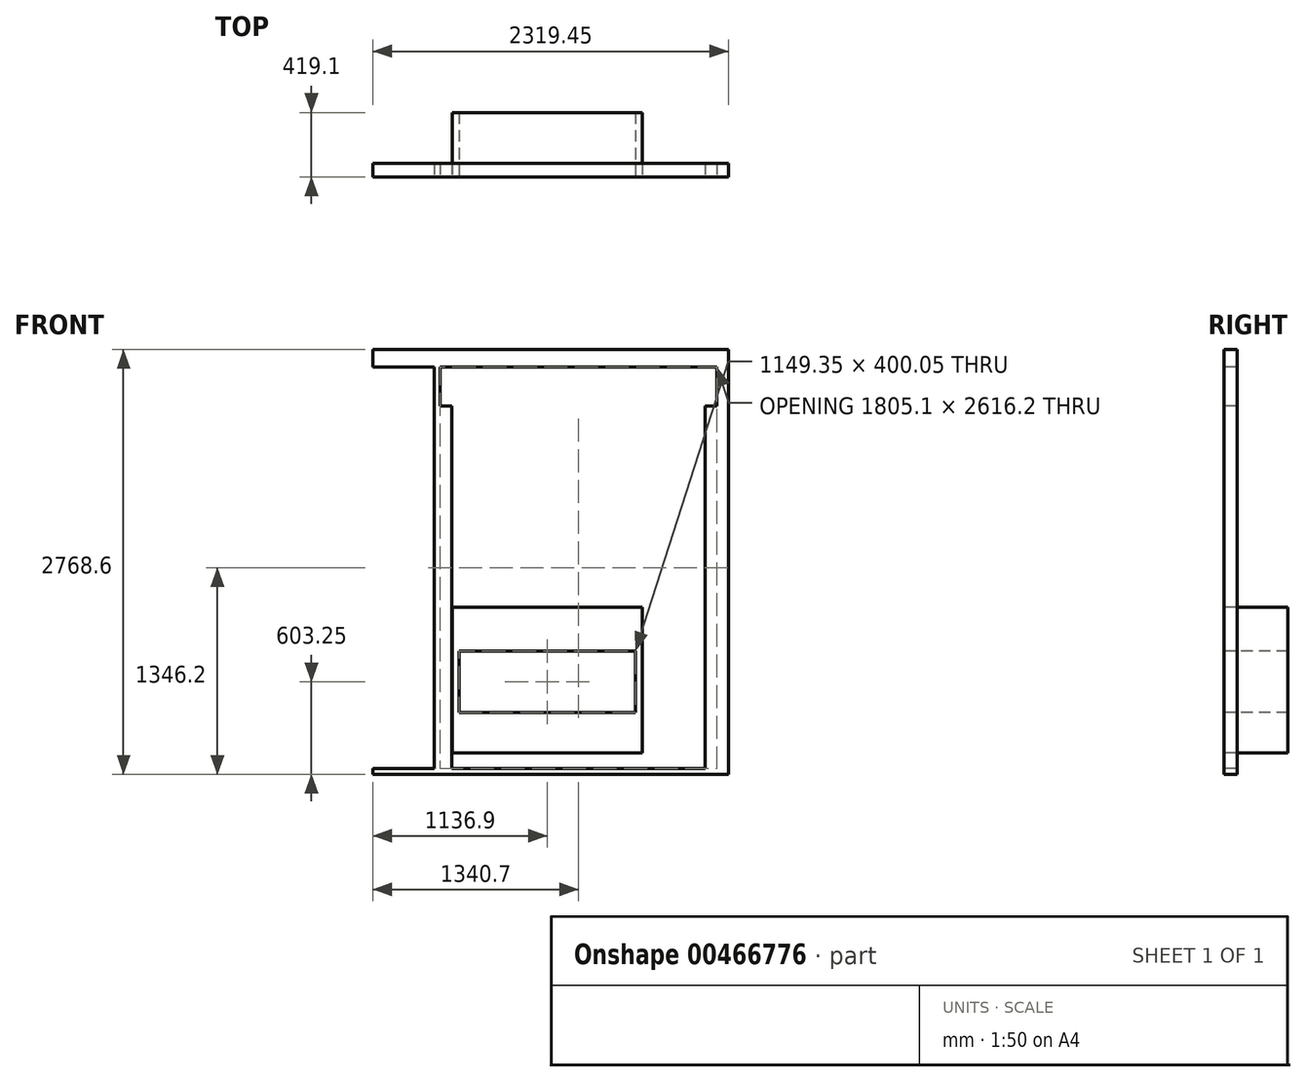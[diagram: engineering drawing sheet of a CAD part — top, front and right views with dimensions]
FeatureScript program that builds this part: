
annotation { "Feature Type Name" : "Feature", "Feature Type Description" : "" }
export const myFeature = defineFeature(function(context is Context, id is Id, definition is map)
    precondition{}
    {
        {
            var Q0;
            Q0=qCreatedBy(makeId("Front.planeOp"),FACE);
            var sketch = newSketch(context, id + "F0", { "sketchPlane" : qUnion([Q0])});
            skLineSegment(sketch, "E0", {"start": v(-619.13, 0) * mm, "end": v(-619.13, 949.33) * mm});
            skLineSegment(sketch, "E1", {"start": v(-619.13, 949.33) * mm, "end": v(619.12, 949.33) * mm});
            skLineSegment(sketch, "E2", {"start": v(619.12, 949.33) * mm, "end": v(619.12, 0) * mm});
            skLineSegment(sketch, "E3", {"start": v(619.12, 0) * mm, "end": v(-619.13, 0) * mm});
            skLineSegment(sketch, "E4.bottom", {"start": v(-574.68, 663.58) * mm, "end": v(574.67, 663.58) * mm});
            skLineSegment(sketch, "E4.top", {"start": v(-574.68, 263.53) * mm, "end": v(574.67, 263.53) * mm});
            skLineSegment(sketch, "E4.left", {"start": v(-574.68, 663.58) * mm, "end": v(-574.68, 263.53) * mm});
            skLineSegment(sketch, "E4.right", {"start": v(574.67, 663.58) * mm, "end": v(574.67, 263.53) * mm});
            skSolve(sketch);
        }
        {
            var Q0;
            Q0=qCreatedBy(makeId("Front.planeOp"),FACE);
            var sketch = newSketch(context, id + "F1", { "sketchPlane" : qUnion([Q0])});
            skLineSegment(sketch, "E5.bottom", {"start": v(-646.25, 38.1) * mm, "end": v(-684.35, 38.1) * mm});
            skLineSegment(sketch, "E5.top", {"start": v(-646.25, 2400.3) * mm, "end": v(-684.35, 2400.3) * mm});
            skLineSegment(sketch, "E5.left", {"start": v(-646.25, 38.1) * mm, "end": v(-646.25, 2400.3) * mm});
            skLineSegment(sketch, "E5.right", {"start": v(-684.35, 38.1) * mm, "end": v(-684.35, 2400.3) * mm});
            skLineSegment(sketch, "E6", {"start": v(-684.35, 38.1) * mm, "end": v(-724.15, 38.1) * mm});
            skLineSegment(sketch, "E7", {"start": v(-724.15, 38.1) * mm, "end": v(-724.15, 2400.3) * mm});
            skLineSegment(sketch, "E8", {"start": v(-724.15, 2400.3) * mm, "end": v(-684.35, 2400.3) * mm});
            skLineSegment(sketch, "E9.bottom", {"start": v(1004.75, 38.1) * mm, "end": v(1042.85, 38.1) * mm});
            skLineSegment(sketch, "E9.top", {"start": v(1004.75, 2400.3) * mm, "end": v(1042.85, 2400.3) * mm});
            skLineSegment(sketch, "E9.left", {"start": v(1004.75, 38.1) * mm, "end": v(1004.75, 2400.3) * mm});
            skLineSegment(sketch, "E9.right", {"start": v(1042.85, 38.1) * mm, "end": v(1042.85, 2400.3) * mm});
            skLineSegment(sketch, "E10", {"start": v(1042.85, 38.1) * mm, "end": v(1080.95, 38.1) * mm});
            skLineSegment(sketch, "E11", {"start": v(1080.95, 38.1) * mm, "end": v(1080.95, 2400.3) * mm});
            skLineSegment(sketch, "E12", {"start": v(1080.95, 2400.3) * mm, "end": v(1042.85, 2400.3) * mm});
            skLineSegment(sketch, "E13", {"start": v(-724.15, 38.1) * mm, "end": v(-762.25, 38.1) * mm});
            skLineSegment(sketch, "E14", {"start": v(-724.15, 2400.3) * mm, "end": v(-724.15, 2654.3) * mm});
            skLineSegment(sketch, "E15", {"start": v(-724.15, 2654.3) * mm, "end": v(-762.25, 2654.3) * mm});
            skLineSegment(sketch, "E16", {"start": v(-646.25, 2400.3) * mm, "end": v(1004.75, 2400.3) * mm});
            skLineSegment(sketch, "E17", {"start": v(-762.25, 38.1) * mm, "end": v(-762.25, 2654.3) * mm});
            skLineSegment(sketch, "E18.bottom", {"start": v(-724.15, 2654.3) * mm, "end": v(1080.95, 2654.3) * mm});
            skLineSegment(sketch, "E18.top", {"start": v(-724.15, 2400.3) * mm, "end": v(1080.95, 2400.3) * mm});
            skLineSegment(sketch, "E18.left", {"start": v(-724.15, 2654.3) * mm, "end": v(-724.15, 2400.3) * mm});
            skLineSegment(sketch, "E18.right", {"start": v(1080.95, 2654.3) * mm, "end": v(1080.95, 2400.3) * mm});
            skLineSegment(sketch, "E19.left", {"start": v(1080.95, 2654.3) * mm, "end": v(1080.95, 38.1) * mm});
            skLineSegment(sketch, "E20.top", {"start": v(1080.95, 38.1) * mm, "end": v(1119.05, 38.1) * mm});
            skLineSegment(sketch, "E21.top", {"start": v(1119.05, 38.1) * mm, "end": v(1157.15, 38.1) * mm});
            skLineSegment(sketch, "E22", {"start": v(1080.95, 2654.3) * mm, "end": v(1119.05, 2654.3) * mm});
            skLineSegment(sketch, "E23", {"start": v(1157.15, 2654.3) * mm, "end": v(1119.05, 2654.3) * mm});
            skLineSegment(sketch, "E24", {"start": v(1119.05, 2654.3) * mm, "end": v(1119.05, 38.1) * mm});
            skLineSegment(sketch, "E25", {"start": v(1119.05, 38.1) * mm, "end": v(1080.95, 38.1) * mm});
            skLineSegment(sketch, "E26", {"start": v(1157.15, 2654.3) * mm, "end": v(1157.15, 38.1) * mm});
            skLineSegment(sketch, "E27.bottom", {"start": v(-1162.3, 2692.4) * mm, "end": v(1157.15, 2692.4) * mm});
            skLineSegment(sketch, "E27.top", {"start": v(-1162.3, 2654.3) * mm, "end": v(1157.15, 2654.3) * mm});
            skLineSegment(sketch, "E27.left", {"start": v(-1162.3, 2692.4) * mm, "end": v(-1162.3, 2654.3) * mm});
            skLineSegment(sketch, "E27.right", {"start": v(1157.15, 2692.4) * mm, "end": v(1157.15, 2654.3) * mm});
            skLineSegment(sketch, "E28.bottom", {"start": v(-1162.3, 2730.5) * mm, "end": v(1157.15, 2730.5) * mm});
            skLineSegment(sketch, "E28.left", {"start": v(-1162.3, 2730.5) * mm, "end": v(-1162.3, 2692.4) * mm});
            skLineSegment(sketch, "E28.right", {"start": v(1157.15, 2730.5) * mm, "end": v(1157.15, 2692.4) * mm});
            skLineSegment(sketch, "E29.bottom", {"start": v(-1162.3, 2768.6) * mm, "end": v(1157.15, 2768.6) * mm});
            skLineSegment(sketch, "E29.left", {"start": v(-1162.3, 2768.6) * mm, "end": v(-1162.3, 2730.5) * mm});
            skLineSegment(sketch, "E29.right", {"start": v(1157.15, 2768.6) * mm, "end": v(1157.15, 2730.5) * mm});
            skLineSegment(sketch, "E30.bottom", {"start": v(-1162.3, 2654.3) * mm, "end": v(-1124.2, 2654.3) * mm});
            skLineSegment(sketch, "E30.top", {"start": v(-1162.3, 38.1) * mm, "end": v(-1124.2, 38.1) * mm});
            skLineSegment(sketch, "E30.left", {"start": v(-1162.3, 2654.3) * mm, "end": v(-1162.3, 38.1) * mm});
            skLineSegment(sketch, "E30.right", {"start": v(-1124.2, 2654.3) * mm, "end": v(-1124.2, 38.1) * mm});
            skLineSegment(sketch, "E31", {"start": v(-1124.2, 38.1) * mm, "end": v(-1162.3, 38.1) * mm});
            skLineSegment(sketch, "E32.bottom", {"start": v(-1124.2, 38.1) * mm, "end": v(-1086.1, 38.1) * mm});
            skLineSegment(sketch, "E32.top", {"start": v(-1124.2, 2654.3) * mm, "end": v(-1086.1, 2654.3) * mm});
            skLineSegment(sketch, "E32.left", {"start": v(-1124.2, 38.1) * mm, "end": v(-1124.2, 2654.3) * mm});
            skLineSegment(sketch, "E32.right", {"start": v(-1086.1, 38.1) * mm, "end": v(-1086.1, 2654.3) * mm});
            skLineSegment(sketch, "E33", {"start": v(-1086.1, 38.1) * mm, "end": v(-1124.2, 38.1) * mm});
            skLineSegment(sketch, "E34.bottom", {"start": v(-1162.3, 38.1) * mm, "end": v(1157.15, 38.1) * mm});
            skLineSegment(sketch, "E34.top", {"start": v(-1162.3, 0) * mm, "end": v(1157.15, 0) * mm});
            skLineSegment(sketch, "E34.left", {"start": v(-1162.3, 38.1) * mm, "end": v(-1162.3, 0) * mm});
            skLineSegment(sketch, "E34.right", {"start": v(1157.15, 38.1) * mm, "end": v(1157.15, 0) * mm});
            skSolve(sketch);
        }
        {
            var Q0;
            Q0=makeQuery(id+"F0.imprint","IMPRINT",FACE,{"disambiguationData":[TD([[makeQuery(id+"F0.imprint","IMPRINT",EDGE,{"derivedFrom":sQuery(id+"F0.wireOp",EDGE,"E0")}),-1.0]])]});
            extrude(context, id + "F2", {"entities" : qUnion([Q0]), "oppositeDirection" : true, "depth" : 419.1 * mm});
        }
        {
            var Q0;
            Q0=makeQuery(id+"F1.imprint","IMPRINT",FACE,{"disambiguationData":[TD([[makeQuery(id+"F1.imprint","IMPRINT",EDGE,{"derivedFrom":sQuery(id+"F1.wireOp",EDGE,"E34.top")}),1.0]])]});
            var Q1;
            {var subQ0=sQuery(id+"F1.wireOp",EDGE,"E24");Q1=makeQuery(id+"F1.imprint","IMPRINT",FACE,{"disambiguationData":[TD([[makeQuery(id+"F1.imprint","IMPRINT",EDGE,{"derivedFrom":subQ0}),1.0]])]});}
            var Q2;
            {var subQ3=sQuery(id+"F1.wireOp",EDGE,"E24");Q2=makeQuery(id+"F1.imprint","IMPRINT",FACE,{"disambiguationData":[TD([[makeQuery(id+"F1.imprint","IMPRINT",EDGE,{"derivedFrom":subQ3}),-1.0]])]});}
            var Q3;
            {var subQ0=sQuery(id+"F1.wireOp",EDGE,"E9.right");Q3=makeQuery(id+"F1.imprint","IMPRINT",FACE,{"disambiguationData":[TD([[makeQuery(id+"F1.imprint","IMPRINT",EDGE,{"derivedFrom":subQ0}),-1.0]])]});}
            var Q4;
            {var subQ0=sQuery(id+"F1.wireOp",EDGE,"E9.left");Q4=makeQuery(id+"F1.imprint","IMPRINT",FACE,{"disambiguationData":[TD([[makeQuery(id+"F1.imprint","IMPRINT",EDGE,{"derivedFrom":subQ0}),-1.0]])]});}
            var Q5;
            Q5=makeQuery(id+"F1.imprint","IMPRINT",FACE,{"disambiguationData":[TD([[makeQuery(id+"F1.imprint","IMPRINT",EDGE,{"derivedFrom":sQuery(id+"F1.wireOp",EDGE,"E29.bottom")}),-1.0]])]});
            var Q6;
            Q6=makeQuery(id+"F1.imprint","IMPRINT",FACE,{"disambiguationData":[TD([[makeQuery(id+"F1.imprint","IMPRINT",EDGE,{"derivedFrom":sQuery(id+"F1.wireOp",EDGE,"E27.bottom")}),1.0]])]});
            var Q7;
            Q7=makeQuery(id+"F1.imprint","IMPRINT",FACE,{"disambiguationData":[TD([[makeQuery(id+"F1.imprint","IMPRINT",EDGE,{"derivedFrom":sQuery(id+"F1.wireOp",EDGE,"E27.left")}),1.0]])]});
            var Q8;
            {var subQ6=sQuery(id+"F1.wireOp",EDGE,"E18.left");Q8=makeQuery(id+"F1.imprint","IMPRINT",FACE,{"disambiguationData":[TD([[makeQuery(id+"F1.imprint","IMPRINT",EDGE,{"derivedFrom":subQ6}),1.0]])]});}
            var Q9;
            {var subQ0=sQuery(id+"F1.wireOp",EDGE,"E5.left");Q9=makeQuery(id+"F1.imprint","IMPRINT",FACE,{"disambiguationData":[TD([[makeQuery(id+"F1.imprint","IMPRINT",EDGE,{"derivedFrom":subQ0}),1.0]])]});}
            var Q10;
            {var subQ0=sQuery(id+"F1.wireOp",EDGE,"E5.right");Q10=makeQuery(id+"F1.imprint","IMPRINT",FACE,{"disambiguationData":[TD([[makeQuery(id+"F1.imprint","IMPRINT",EDGE,{"derivedFrom":subQ0}),1.0]])]});}
            var Q11;
            {var subQ3=sQuery(id+"F1.wireOp",EDGE,"E7");Q11=makeQuery(id+"F1.imprint","IMPRINT",FACE,{"disambiguationData":[TD([[makeQuery(id+"F1.imprint","IMPRINT",EDGE,{"derivedFrom":subQ3}),1.0]])]});}
            var Q12;
            Q12=makeQuery(id+"F1.imprint","IMPRINT",FACE,{"disambiguationData":[TD([[makeQuery(id+"F1.imprint","IMPRINT",EDGE,{"derivedFrom":sQuery(id+"F1.wireOp",EDGE,"E32.top")}),-1.0]])]});
            var Q13;
            Q13=makeQuery(id+"F1.imprint","IMPRINT",FACE,{"disambiguationData":[TD([[makeQuery(id+"F1.imprint","IMPRINT",EDGE,{"derivedFrom":sQuery(id+"F1.wireOp",EDGE,"E30.bottom")}),-1.0]])]});
            extrude(context, id + "F3", {"entities" : qUnion([Q0, Q1, Q2, Q3, Q4, Q5, Q6, Q7, Q8, Q9, Q10, Q11, Q12, Q13]), "oppositeDirection" : true, "depth" : 88.9 * mm});
        }
        {
            var Q0;
            Q0=makeQuery(id+"F2.opExtrude","SWEPT_BODY",BODY,{"disambiguationData":[OSD([sQuery(id+"F0.wireOp",EDGE,"E0"),sQuery(id+"F0.wireOp",EDGE,"E1"),sQuery(id+"F0.wireOp",EDGE,"E2"),sQuery(id+"F0.wireOp",EDGE,"E3"),sQuery(id+"F0.wireOp",EDGE,"E4.bottom"),sQuery(id+"F0.wireOp",EDGE,"E4.top"),sQuery(id+"F0.wireOp",EDGE,"E4.left"),sQuery(id+"F0.wireOp",EDGE,"E4.right")])]});
            transform(context, id + "F4", {"entities" : qUnion([Q0]), "transformType" : TransformType.TRANSLATION_3D, "dx" : -25.4 * mm, "dy" : 0 * mm, "dz" : 139.7 * mm, "makeCopy" : false});
        }
    });
